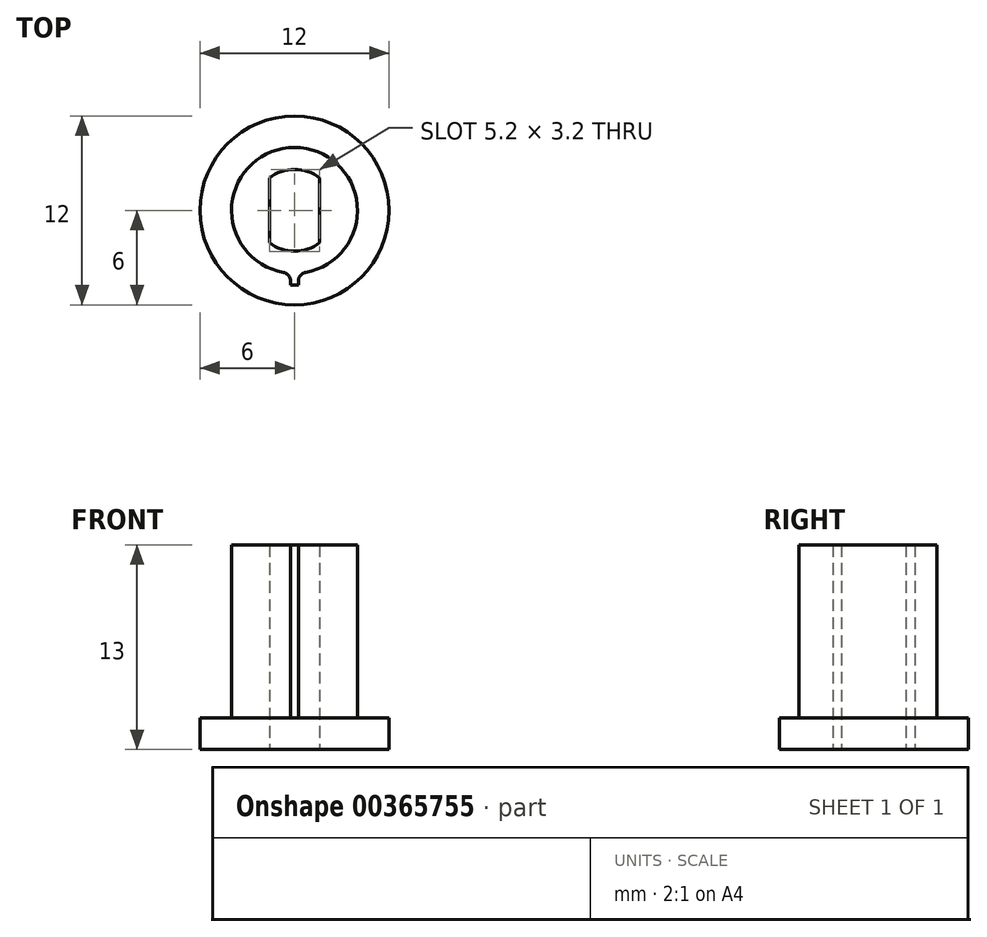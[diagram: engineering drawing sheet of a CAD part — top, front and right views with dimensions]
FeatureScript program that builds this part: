
annotation { "Feature Type Name" : "Feature", "Feature Type Description" : "" }
export const myFeature = defineFeature(function(context is Context, id is Id, definition is map)
    precondition{}
    {
        {
            assignVariable(context, id + "F0", {"name" : "Pulley_height", "anyValue" : 13});
        }
        {
            var Q0;
            Q0=qCreatedBy(makeId("Top.planeOp"),FACE);
            var sketch = newSketch(context, id + "F1", { "sketchPlane" : qUnion([Q0])});
            skCircle(sketch, "E0", {"center": v(0, 0) * mm, "radius": 4.75 * mm, "construction": true});
            skCircle(sketch, "E1", {"center": v(0, 0) * mm, "radius": 6 * mm});
            skLineSegment(sketch, "E2", {"start": v(0, -4.75) * mm, "end": v(0, 0) * mm, "construction": true});
            skLineSegment(sketch, "E3.bottom", {"start": v(-0.25, -4) * mm, "end": v(0.25, -4) * mm});
            skLineSegment(sketch, "E3.top", {"start": v(-0.25, -4.74) * mm, "end": v(0.25, -4.74) * mm});
            skLineSegment(sketch, "E3.left", {"start": v(-0.25, -4.48) * mm, "end": v(-0.25, -4.74) * mm});
            skLineSegment(sketch, "E3.right", {"start": v(0.25, -4.48) * mm, "end": v(0.25, -4.74) * mm});
            skPoint(sketch, "E3.middle", {"position": v(0, -4.37) * mm});
            skArc(sketch, "E4", {"start": v(0.7, -3.94) * mm, "mid": v(-0.23, 4) * mm, "end": v(-0.25, -4) * mm});
            skPoint(sketch, "E5.visualSharp", {"position": v(0.25, -4) * mm});
            skArc(sketch, "E5.filletArc", {"start": v(0.7, -3.94) * mm, "mid": v(0.38, -4.13) * mm, "end": v(0.25, -4.48) * mm});
            skArc(sketch, "E6.MirrorCS", {"start": v(-0.7, -3.94) * mm, "mid": v(-0.38, -4.13) * mm, "end": v(-0.25, -4.48) * mm});
            skLineSegment(sketch, "E7", {"start": v(0.7, -3.94) * mm, "end": v(0.25, -4) * mm});
            skCircle(sketch, "E8", {"center": v(0, 0) * mm, "radius": 2.6 * mm});
            skLineSegment(sketch, "E9", {"start": v(1.6, -2.05) * mm, "end": v(1.6, 2.05) * mm});
            skLineSegment(sketch, "E10.MirrorCS", {"start": v(-1.6, -2.05) * mm, "end": v(-1.6, 2.05) * mm});
            skSolve(sketch);
        }
        {
            var Q0;
            {var subQ3=sQuery(id+"F1.wireOp",EDGE,"E3.bottom");Q0=makeQuery(id+"F1.imprint","IMPRINT",FACE,{"disambiguationData":[TD([[makeQuery(id+"F1.imprint","IMPRINT",EDGE,{"derivedFrom":subQ3}),1.0]])]});}
            var Q1;
            {var subQ0=sQuery(id+"F1.wireOp",EDGE,"E9");Q1=makeQuery(id+"F1.imprint","IMPRINT",FACE,{"disambiguationData":[TD([[makeQuery(id+"F1.imprint","IMPRINT",EDGE,{"derivedFrom":subQ0}),-1.0]])]});}
            var Q2;
            {var subQ0=sQuery(id+"F1.wireOp",EDGE,"E10.MirrorCS");Q2=makeQuery(id+"F1.imprint","IMPRINT",FACE,{"disambiguationData":[TD([[makeQuery(id+"F1.imprint","IMPRINT",EDGE,{"derivedFrom":subQ0}),1.0]])]});}
            extrude(context, id + "F2", {"entities" : qUnion([Q0, Q1, Q2]), "depth" : (getVariable(context, 'Pulley_height')) * mm});
        }
        {
            var Q0;
            Q0=makeQuery(id+"F1.imprint","IMPRINT",FACE,{"disambiguationData":[TD([[makeQuery(id+"F1.imprint","IMPRINT",EDGE,{"derivedFrom":sQuery(id+"F1.wireOp",EDGE,"E1")}),1.0]])]});
            var Q1;
            Q1=sQuery(id+"F1.wireOp",EDGE,"E1");
            extrude(context, id + "F3", {"entities" : qUnion([Q0]), "operationType" : NewBodyOperationType.ADD, "surfaceEntities" : qUnion([Q1]), "depth" : 2 * mm});
        }
        {
            var Q0;
            {var subQ0=sQuery(id+"F1.wireOp",EDGE,"E3.bottom");Q0=makeQuery(id+"F1.imprint","IMPRINT",FACE,{"disambiguationData":[TD([[makeQuery(id+"F1.imprint","IMPRINT",EDGE,{"derivedFrom":subQ0}),-1.0]])]});}
            extrude(context, id + "F4", {"entities" : qUnion([Q0]), "operationType" : NewBodyOperationType.ADD, "depth" : (getVariable(context, 'Pulley_height')) * mm});
        }
        {
            var Q0;
            Q0=qCreatedBy(makeId("Top.planeOp"),FACE);
            cPlane(context, id + "F5", {"entities" : qUnion([Q0]), "cplaneType" : CPlaneType.OFFSET, "offset" : (getVariable(context, 'Pulley_height') / 2) * mm, "width" : 150 * mm, "height" : 150 * mm});
        }
    });
